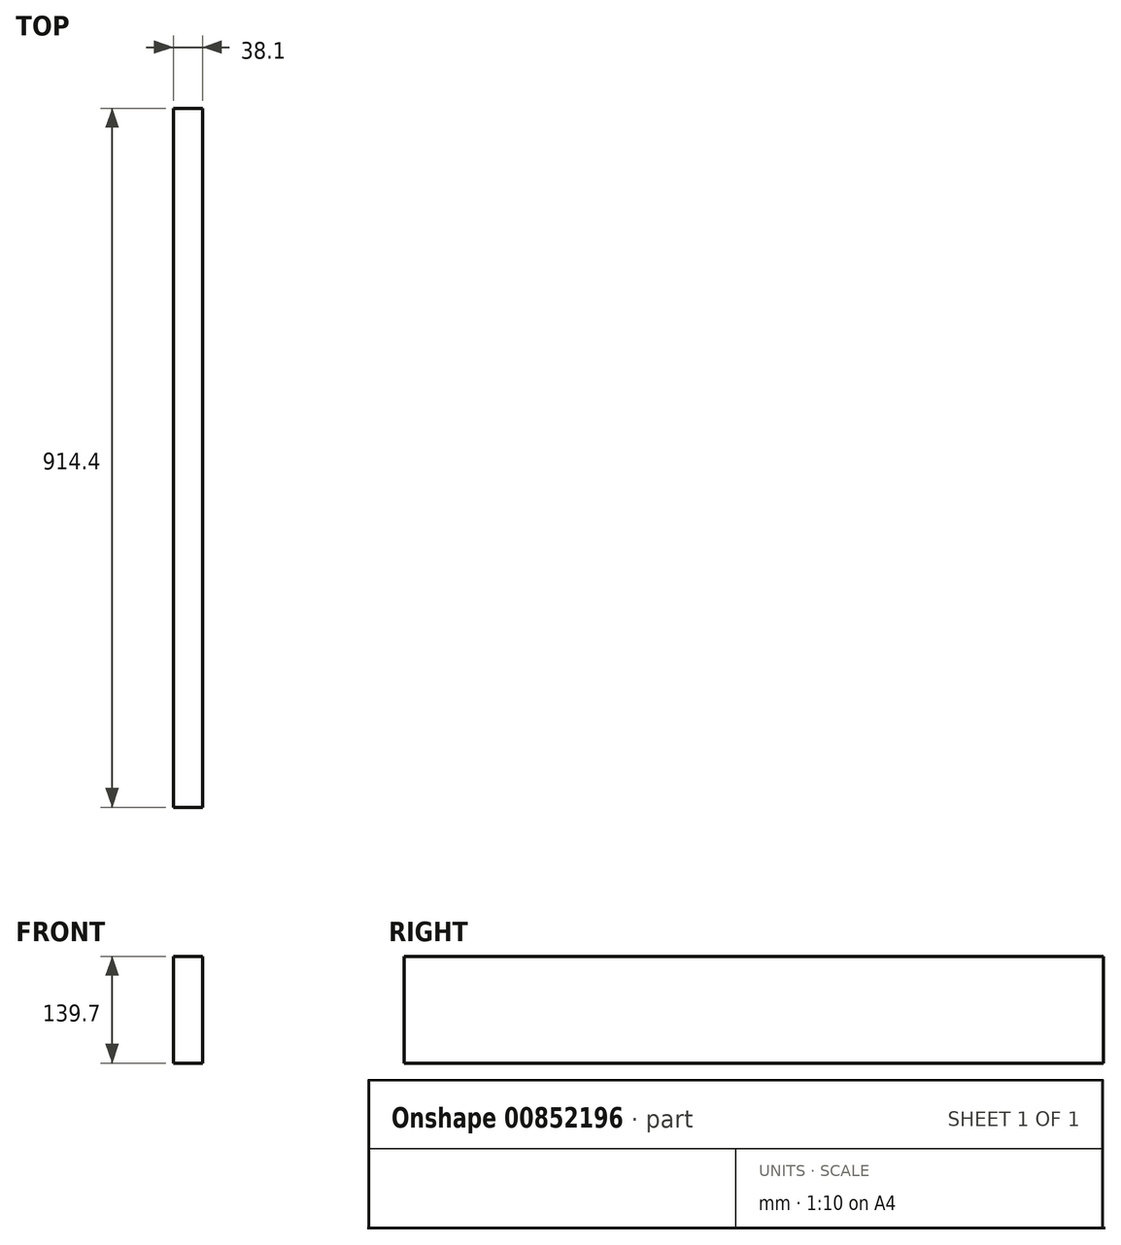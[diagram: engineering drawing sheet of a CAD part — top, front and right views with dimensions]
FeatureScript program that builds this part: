
annotation { "Feature Type Name" : "Feature", "Feature Type Description" : "" }
export const myFeature = defineFeature(function(context is Context, id is Id, definition is map)
    precondition{}
    {
        {
            var Q0;
            Q0=qCreatedBy(makeId("Front.planeOp"),FACE);
            var sketch = newSketch(context, id + "F0", { "sketchPlane" : qUnion([Q0])});
            skLineSegment(sketch, "E0.bottom", {"start": v(19.05, -69.85) * mm, "end": v(-19.05, -69.85) * mm});
            skLineSegment(sketch, "E0.top", {"start": v(19.05, 69.85) * mm, "end": v(-19.05, 69.85) * mm});
            skLineSegment(sketch, "E0.left", {"start": v(19.05, -69.85) * mm, "end": v(19.05, 69.85) * mm});
            skLineSegment(sketch, "E0.right", {"start": v(-19.05, -69.85) * mm, "end": v(-19.05, 69.85) * mm});
            skPoint(sketch, "E0.middle", {"position": v(0, 0) * mm});
            skSolve(sketch);
        }
        {
            var Q0;
            Q0=qSketchRegion(id+"F0",true);
            extrude(context, id + "F1", {"entities" : qUnion([Q0]), "depth" : 914.4 * mm, "offsetDistance" : 25.4 * mm});
        }
    });
